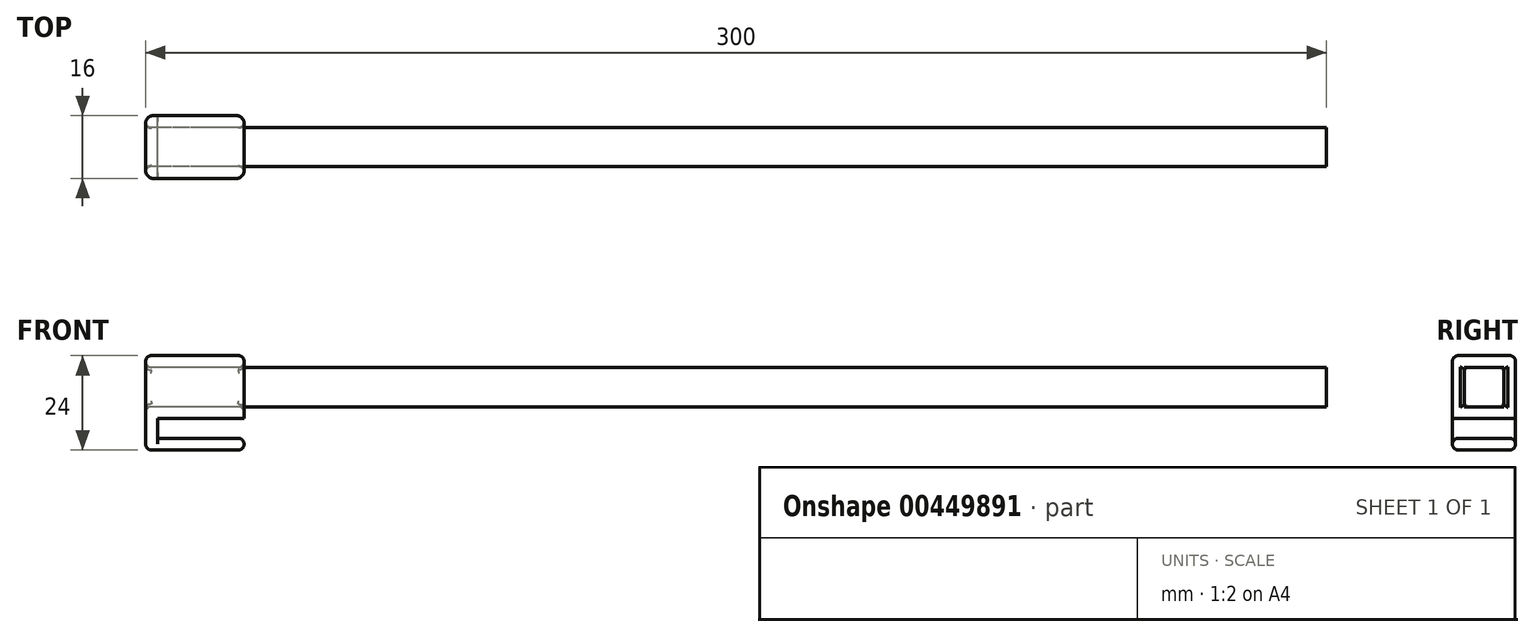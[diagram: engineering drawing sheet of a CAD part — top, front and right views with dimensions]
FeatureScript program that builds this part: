
annotation { "Feature Type Name" : "Feature", "Feature Type Description" : "" }
export const myFeature = defineFeature(function(context is Context, id is Id, definition is map)
    precondition{}
    {
        {
            var Q0;
            Q0=qCreatedBy(makeId("Right.planeOp"),FACE);
            var sketch = newSketch(context, id + "F0", { "sketchPlane" : qUnion([Q0])});
            skLineSegment(sketch, "E0.bottom", {"start": v(5, 5) * mm, "end": v(-5, 5) * mm});
            skLineSegment(sketch, "E0.top", {"start": v(5, -5) * mm, "end": v(-5, -5) * mm});
            skLineSegment(sketch, "E0.left", {"start": v(5, 5) * mm, "end": v(5, -5) * mm});
            skLineSegment(sketch, "E0.right", {"start": v(-5, 5) * mm, "end": v(-5, -5) * mm});
            skPoint(sketch, "E0.middle", {"position": v(0, 0) * mm});
            skSolve(sketch);
        }
        {
            var Q0;
            Q0 = qSketchRegion(id + "F0", true);
            extrude(context, id + "F1", {"entities" : qUnion([Q0]), "depth" : 300 * mm});
        }
        {
            var Q0;
            Q0=qCreatedBy(makeId("Right.planeOp"),FACE);
            var sketch = newSketch(context, id + "F2", { "sketchPlane" : qUnion([Q0])});
            skLineSegment(sketch, "E1.bottom", {"start": v(5, -5) * mm, "end": v(-5, -5) * mm});
            skLineSegment(sketch, "E1.top", {"start": v(5, 5) * mm, "end": v(-5, 5) * mm});
            skLineSegment(sketch, "E1.left", {"start": v(5, -5) * mm, "end": v(5, 5) * mm});
            skLineSegment(sketch, "E1.right", {"start": v(-5, -5) * mm, "end": v(-5, 5) * mm});
            skPoint(sketch, "E1.middle", {"position": v(0, 0) * mm});
            skLineSegment(sketch, "E2.0", {"start": v(-8, -8) * mm, "end": v(-8, 8) * mm});
            skLineSegment(sketch, "E2.1", {"start": v(8, -8) * mm, "end": v(-8, -8) * mm});
            skLineSegment(sketch, "E2.2", {"start": v(8, -8) * mm, "end": v(8, 8) * mm});
            skLineSegment(sketch, "E2.3", {"start": v(8, 8) * mm, "end": v(-8, 8) * mm});
            skSolve(sketch);
        }
        {
            var Q0;
            Q0 = qSketchRegion(id + "F2", true);
            extrude(context, id + "F3", {"entities" : qUnion([Q0]), "depth" : 25 * mm});
        }
        {
            var Q0;
            Q0=makeQuery(id+"F3.opExtrude","SWEPT_FACE",FACE,{"disambiguationData":[OSD([sQuery(id+"F2.wireOp",EDGE,"E2.1")])]});
            var sketch = newSketch(context, id + "F4", { "sketchPlane" : qUnion([Q0])});
            skLineSegment(sketch, "E3.bottom", {"start": v(0, 8) * mm, "end": v(3, 8) * mm});
            skLineSegment(sketch, "E3.top", {"start": v(0, -8) * mm, "end": v(3, -8) * mm});
            skLineSegment(sketch, "E3.left", {"start": v(0, 8) * mm, "end": v(0, -8) * mm});
            skLineSegment(sketch, "E3.right", {"start": v(3, 8) * mm, "end": v(3, -8) * mm});
            skSolve(sketch);
        }
        {
            var Q0;
            Q0 = qSketchRegion(id + "F4", true);
            extrude(context, id + "F5", {"entities" : qUnion([Q0]), "operationType" : NewBodyOperationType.ADD, "depth" : 5 * mm});
        }
        {
            var Q0;
            Q0=makeQuery(id+"F5.opExtrude","CAP_FACE",FACE,{"disambiguationData":[OSD([sQuery(id+"F4.wireOp",EDGE,"E3.bottom"),sQuery(id+"F4.wireOp",EDGE,"E3.top"),sQuery(id+"F4.wireOp",EDGE,"E3.left"),sQuery(id+"F4.wireOp",EDGE,"E3.right")])],"isStart":false});
            var sketch = newSketch(context, id + "F6", { "sketchPlane" : qUnion([Q0])});
            skLineSegment(sketch, "E4.bottom", {"start": v(0, 8) * mm, "end": v(25, 8) * mm});
            skLineSegment(sketch, "E4.top", {"start": v(0, -8) * mm, "end": v(25, -8) * mm});
            skLineSegment(sketch, "E4.left", {"start": v(0, 8) * mm, "end": v(0, -8) * mm});
            skLineSegment(sketch, "E4.right", {"start": v(25, 8) * mm, "end": v(25, -8) * mm});
            skSolve(sketch);
        }
        {
            var Q0;
            Q0 = qSketchRegion(id + "F6", true);
            extrude(context, id + "F7", {"entities" : qUnion([Q0]), "operationType" : NewBodyOperationType.ADD, "depth" : 3 * mm});
        }
        {
            var Q0;
            Q0=makeQuery(id+"F7.opExtrude","SWEPT_EDGE",EDGE,{"disambiguationData":[OSD([sQuery(id+"F6.wireOp",EDGE,"E4.bottom"),sQuery(id+"F6.wireOp",EDGE,"E4.right")])]});
            var Q1;
            Q1=makeQuery(id+"F7.opExtrude","SWEPT_EDGE",EDGE,{"disambiguationData":[OSD([sQuery(id+"F6.wireOp",EDGE,"E4.top"),sQuery(id+"F6.wireOp",EDGE,"E4.right")])]});
            var Q2;
            Q2=makeQuery(id+"F5.opExtrude","CAP_EDGE",EDGE,{"disambiguationData":[OSD([sQuery(id+"F4.wireOp",EDGE,"E3.right")])],"isStart":false});
            var Q3;
            Q3=makeQuery(id+"F5.opExtrude","CAP_EDGE",EDGE,{"disambiguationData":[OSD([sQuery(id+"F4.wireOp",EDGE,"E3.right")])],"isStart":true});
            var Q4;
            Q4=makeQuery(id+"F3.opExtrude","CAP_EDGE",EDGE,{"disambiguationData":[OSD([sQuery(id+"F2.wireOp",EDGE,"E2.0")])],"isStart":false});
            var Q5;
            Q5=makeQuery(id+"F3.opExtrude","CAP_EDGE",EDGE,{"disambiguationData":[OSD([sQuery(id+"F2.wireOp",EDGE,"E2.2")])],"isStart":false});
            var Q6;
            Q6=makeQuery(id+"F7.boolean.opBoolean","MERGE",EDGE,{"derivedFrom":[makeQuery(id+"F5.boolean.opBoolean","MERGE",EDGE,{"derivedFrom":[makeQuery(id+"F3.opExtrude","CAP_EDGE",EDGE,{"disambiguationData":[OSD([sQuery(id+"F2.wireOp",EDGE,"E2.0")])],"isStart":true}),makeQuery(id+"F5.opExtrude","SWEPT_EDGE",EDGE,{"disambiguationData":[OSD([sQuery(id+"F4.wireOp",EDGE,"E3.bottom"),sQuery(id+"F4.wireOp",EDGE,"E3.left")])]})]}),makeQuery(id+"F7.opExtrude","SWEPT_EDGE",EDGE,{"disambiguationData":[OSD([sQuery(id+"F6.wireOp",EDGE,"E4.bottom"),sQuery(id+"F6.wireOp",EDGE,"E4.left")])]})]});
            var Q7;
            Q7=makeQuery(id+"F7.boolean.opBoolean","MERGE",EDGE,{"derivedFrom":[makeQuery(id+"F5.boolean.opBoolean","MERGE",EDGE,{"derivedFrom":[makeQuery(id+"F3.opExtrude","CAP_EDGE",EDGE,{"disambiguationData":[OSD([sQuery(id+"F2.wireOp",EDGE,"E2.2")])],"isStart":true}),makeQuery(id+"F5.opExtrude","SWEPT_EDGE",EDGE,{"disambiguationData":[OSD([sQuery(id+"F4.wireOp",EDGE,"E3.top"),sQuery(id+"F4.wireOp",EDGE,"E3.left")])]})]}),makeQuery(id+"F7.opExtrude","SWEPT_EDGE",EDGE,{"disambiguationData":[OSD([sQuery(id+"F6.wireOp",EDGE,"E4.top"),sQuery(id+"F6.wireOp",EDGE,"E4.left")])]})]});
            fillet(context, id + "F8", {"entities" : qUnion([Q0, Q1, Q2, Q3, Q4, Q5, Q6, Q7]), "radius" : 2 * mm, "tangentPropagation" : true, "allowEdgeOverflow" : false});
        }
        {
            var Q0;
            Q0=makeQuery(id+"F3.opExtrude","SWEPT_EDGE",EDGE,{"disambiguationData":[OSD([sQuery(id+"F2.wireOp",EDGE,"E2.0"),sQuery(id+"F2.wireOp",EDGE,"E2.3")])]});
            var Q1;
            Q1=makeQuery(id+"F7.opExtrude","CAP_EDGE",EDGE,{"disambiguationData":[OSD([sQuery(id+"F6.wireOp",EDGE,"E4.bottom")])],"isStart":false});
            var Q2;
            Q2=makeQuery(id+"F7.opExtrude","CAP_EDGE",EDGE,{"disambiguationData":[OSD([sQuery(id+"F6.wireOp",EDGE,"E4.bottom")])],"isStart":true});
            fillet(context, id + "F9", {"entities" : qUnion([Q0, Q1, Q2]), "radius" : 1.5 * mm, "tangentPropagation" : true, "allowEdgeOverflow" : false});
        }
        {
            var Q0;
            Q0=makeQuery(id+"F3.opExtrude","SWEPT_EDGE",EDGE,{"disambiguationData":[OSD([sQuery(id+"F2.wireOp",EDGE,"E1.top"),sQuery(id+"F2.wireOp",EDGE,"E1.left")])]});
            var Q1;
            Q1=makeQuery(id+"F3.opExtrude","SWEPT_EDGE",EDGE,{"disambiguationData":[OSD([sQuery(id+"F2.wireOp",EDGE,"E1.top"),sQuery(id+"F2.wireOp",EDGE,"E1.right")])]});
            var Q2;
            Q2=makeQuery(id+"F3.opExtrude","SWEPT_EDGE",EDGE,{"disambiguationData":[OSD([sQuery(id+"F2.wireOp",EDGE,"E1.bottom"),sQuery(id+"F2.wireOp",EDGE,"E1.right")])]});
            var Q3;
            Q3=makeQuery(id+"F3.opExtrude","SWEPT_EDGE",EDGE,{"disambiguationData":[OSD([sQuery(id+"F2.wireOp",EDGE,"E1.bottom"),sQuery(id+"F2.wireOp",EDGE,"E1.left")])]});
            fillet(context, id + "F10", {"entities" : qUnion([Q0, Q1, Q2, Q3]), "radius" : 1.5 * mm, "tangentPropagation" : true, "allowEdgeOverflow" : false});
        }
        {
            var Q0;
            Q0=makeQuery(id+"F3.opExtrude","CAP_EDGE",EDGE,{"disambiguationData":[OSD([sQuery(id+"F2.wireOp",EDGE,"E1.right")])],"isStart":false});
            var Q1;
            Q1=makeQuery(id+"F3.opExtrude","CAP_EDGE",EDGE,{"disambiguationData":[OSD([sQuery(id+"F2.wireOp",EDGE,"E1.top")])],"isStart":true});
            fillet(context, id + "F11", {"entities" : qUnion([Q0, Q1]), "radius" : 1.5 * mm, "tangentPropagation" : true, "allowEdgeOverflow" : false});
        }
    });
